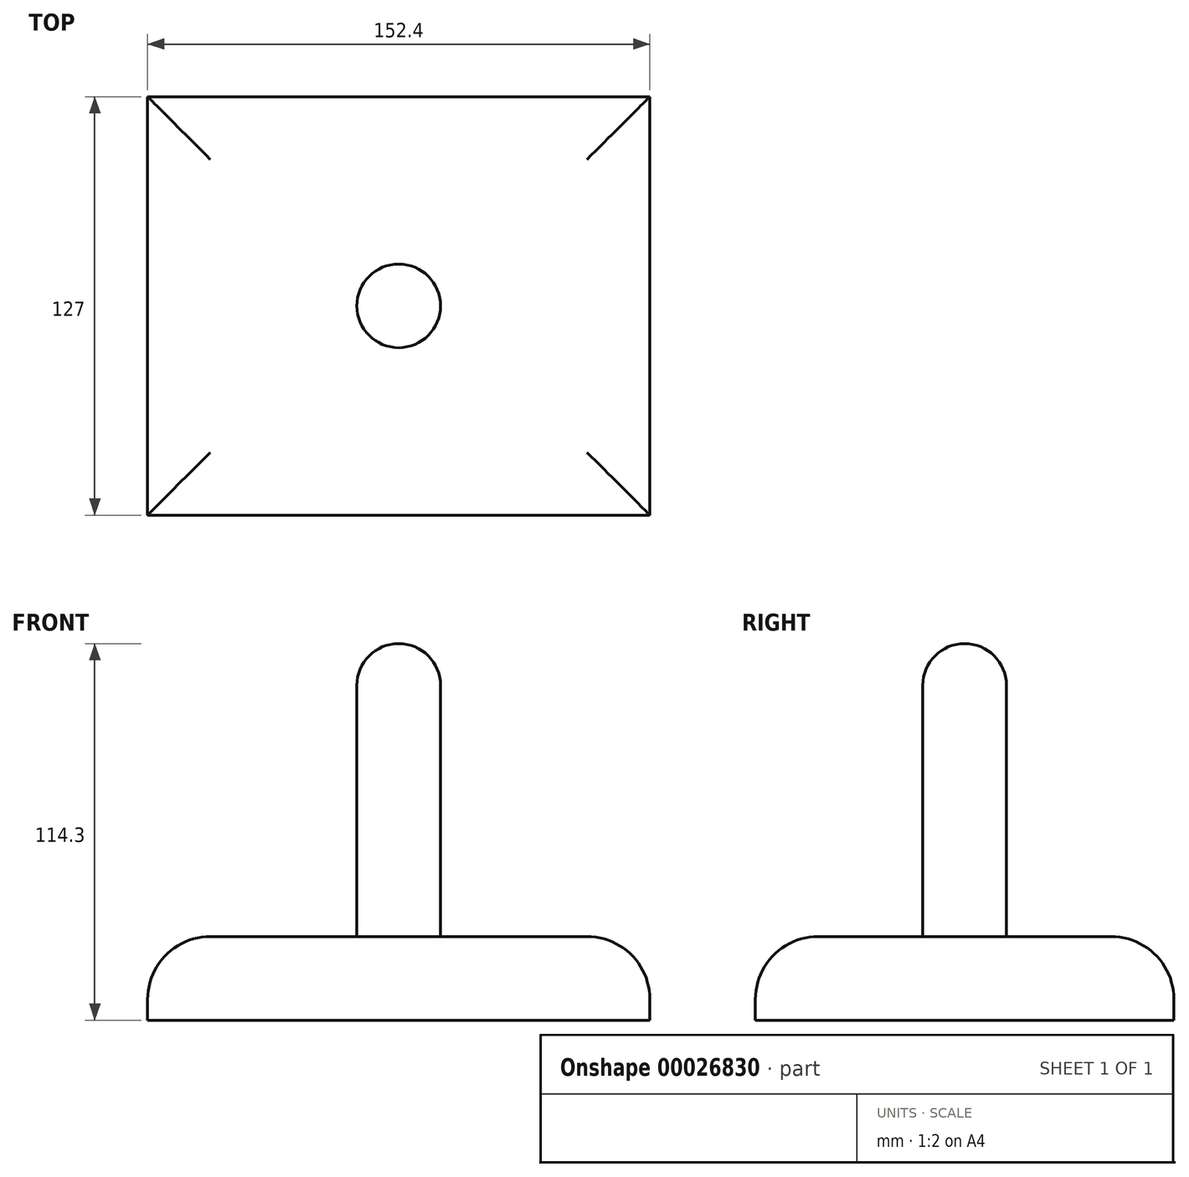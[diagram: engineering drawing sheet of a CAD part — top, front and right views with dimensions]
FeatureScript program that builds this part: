
annotation { "Feature Type Name" : "Feature", "Feature Type Description" : "" }
export const myFeature = defineFeature(function(context is Context, id is Id, definition is map)
    precondition{}
    {
        {
            var Q0;
            Q0=qCreatedBy(makeId("Top.planeOp"),FACE);
            var sketch = newSketch(context, id + "F0", { "sketchPlane" : qUnion([Q0])});
            skLineSegment(sketch, "E0.rect.bottom", {"start": v(-76.2, 63.5) * mm, "end": v(76.2, 63.5) * mm});
            skLineSegment(sketch, "E0.rect.top", {"start": v(-76.2, -63.5) * mm, "end": v(76.2, -63.5) * mm});
            skLineSegment(sketch, "E0.rect.left", {"start": v(-76.2, 63.5) * mm, "end": v(-76.2, -63.5) * mm});
            skLineSegment(sketch, "E0.rect.right", {"start": v(76.2, 63.5) * mm, "end": v(76.2, -63.5) * mm});
            skPoint(sketch, "E0.rect.middle", {"position": v(0, 0) * mm});
            skSolve(sketch);
        }
        {
            var Q0;
            Q0=makeQuery(id+"F0.imprint","IMPRINT",FACE,{"disambiguationData":[TD([[makeQuery(id+"F0.imprint","IMPRINT",EDGE,{"derivedFrom":sQuery(id+"F0.wireOp",EDGE,"E0.rect.bottom")}),-1.0]])]});
            extrude(context, id + "F1", {"entities" : qUnion([Q0]), "depth" : 25.4 * mm});
        }
        {
            var Q0;
            Q0=makeQuery(id+"F1.opExtrude","CAP_FACE",FACE,{"disambiguationData":[OSD([sQuery(id+"F0.wireOp",EDGE,"E0.rect.bottom"),sQuery(id+"F0.wireOp",EDGE,"E0.rect.top"),sQuery(id+"F0.wireOp",EDGE,"E0.rect.left"),sQuery(id+"F0.wireOp",EDGE,"E0.rect.right")])],"isStart":false});
            var sketch = newSketch(context, id + "F2", { "sketchPlane" : qUnion([Q0])});
            skCircle(sketch, "E1", {"center": v(0, 0) * mm, "radius": 12.7 * mm});
            skSolve(sketch);
        }
        {
            var Q0;
            Q0=makeQuery(id+"F2.imprint","IMPRINT",FACE,{"disambiguationData":[TD([[makeQuery(id+"F2.imprint","IMPRINT",EDGE,{"derivedFrom":sQuery(id+"F2.wireOp",EDGE,"E1")}),1.0]])]});
            extrude(context, id + "F3", {"entities" : qUnion([Q0]), "operationType" : NewBodyOperationType.ADD, "depth" : 76.2 * mm});
        }
        {
            var Q0;
            Q0=makeQuery(id+"F3.opExtrude","CAP_FACE",FACE,{"disambiguationData":[OSD([sQuery(id+"F2.wireOp",EDGE,"E1")])],"isStart":false});
            var sketch = newSketch(context, id + "F4", { "sketchPlane" : qUnion([Q0])});
            skLineSegment(sketch, "E2", {"start": v(0, 12.7) * mm, "end": v(0, -12.7) * mm});
            skSolve(sketch);
        }
        {
            var Q0;
            {var subQ1=sQuery(id+"F4.wireOp",EDGE,"E2");Q0=makeQuery(id+"F4.imprint","IMPRINT",FACE,{"disambiguationData":[TD([[makeQuery(id+"F4.imprint","IMPRINT",EDGE,{"derivedFrom":subQ1}),1.0]])]});}
            var Q1;
            Q1=sQuery(id+"F4.wireOp",EDGE,"E2");
            revolve(context, id + "F5", {"operationType" : NewBodyOperationType.ADD, "entities" : qUnion([Q0]), "axis" : qUnion([Q1]), "revolveType" : RevolveType.FULL});
        }
        {
            var Q0;
            Q0=makeQuery(id+"F1.opExtrude","CAP_EDGE",EDGE,{"disambiguationData":[OSD([sQuery(id+"F0.wireOp",EDGE,"E0.rect.top")])],"isStart":false});
            var Q1;
            Q1=makeQuery(id+"F1.opExtrude","CAP_EDGE",EDGE,{"disambiguationData":[OSD([sQuery(id+"F0.wireOp",EDGE,"E0.rect.right")])],"isStart":false});
            var Q2;
            Q2=makeQuery(id+"F1.opExtrude","CAP_EDGE",EDGE,{"disambiguationData":[OSD([sQuery(id+"F0.wireOp",EDGE,"E0.rect.bottom")])],"isStart":false});
            var Q3;
            Q3=makeQuery(id+"F1.opExtrude","CAP_EDGE",EDGE,{"disambiguationData":[OSD([sQuery(id+"F0.wireOp",EDGE,"E0.rect.left")])],"isStart":false});
            fillet(context, id + "F6", {"entities" : qUnion([Q0, Q1, Q2, Q3]), "radius" : 19.05 * mm, "tangentPropagation" : true, "allowEdgeOverflow" : false});
        }
    });
